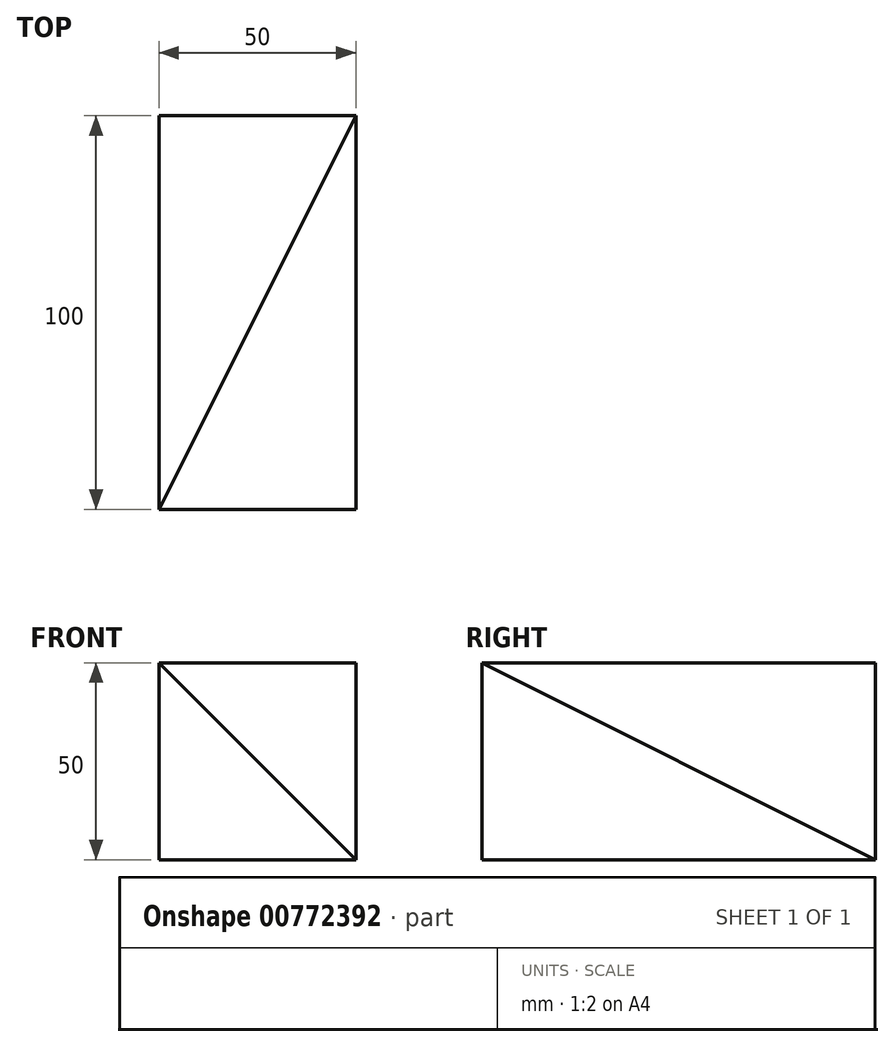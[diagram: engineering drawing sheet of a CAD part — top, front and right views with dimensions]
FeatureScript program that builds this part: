
annotation { "Feature Type Name" : "Feature", "Feature Type Description" : "" }
export const myFeature = defineFeature(function(context is Context, id is Id, definition is map)
    precondition{}
    {
        {
            var Q0;
            Q0=qCreatedBy(makeId("Front.planeOp"),FACE);
            var sketch = newSketch(context, id + "F0", { "sketchPlane" : qUnion([Q0])});
            skLineSegment(sketch, "E0", {"start": v(0, 0) * mm, "end": v(0, 50) * mm});
            skLineSegment(sketch, "E1", {"start": v(0, 50) * mm, "end": v(50, 0) * mm});
            skLineSegment(sketch, "E2", {"start": v(50, 0) * mm, "end": v(0, 0) * mm});
            skSolve(sketch);
        }
        {
            var Q0;
            Q0=makeQuery(id+"F0.imprint","IMPRINT",FACE,{"disambiguationData":[TD([[makeQuery(id+"F0.imprint","IMPRINT",EDGE,{"derivedFrom":sQuery(id+"F0.wireOp",EDGE,"E0")}),-1.0]])]});
            extrude(context, id + "F1", {"entities" : qUnion([Q0]), "depth" : 100 * mm, "offsetDistance" : 25 * mm});
        }
        {
            var Q0;
            Q0=makeQuery(id+"F1.opExtrude","SWEPT_FACE",FACE,{"disambiguationData":[OSD([sQuery(id+"F0.wireOp",EDGE,"E2")])]});
            var sketch = newSketch(context, id + "F2", { "sketchPlane" : qUnion([Q0])});
            skLineSegment(sketch, "E3", {"start": v(0, 0) * mm, "end": v(0, 100) * mm});
            skLineSegment(sketch, "E4", {"start": v(0, 100) * mm, "end": v(50, 0) * mm});
            skLineSegment(sketch, "E5", {"start": v(50, 0) * mm, "end": v(0, 0) * mm});
            skSolve(sketch);
        }
        {
            var Q0;
            Q0=qSketchRegion(id+"F2",true);
            var Q1;
            Q1=makeQuery(id+"F1.opExtrude","CAP_VERTEX",VERTEX,{"disambiguationData":[OSD([sQuery(id+"F0.wireOp",EDGE,"E0"),sQuery(id+"F0.wireOp",EDGE,"E1")])],"isStart":true});
            extrude(context, id + "F3", {"entities" : qUnion([Q0]), "operationType" : NewBodyOperationType.ADD, "endBound" : BoundingType.UP_TO_VERTEX, "oppositeDirection" : true, "depth" : 25 * mm, "endBoundEntityVertex" : qUnion([Q1]), "offsetDistance" : 25 * mm});
        }
    });
